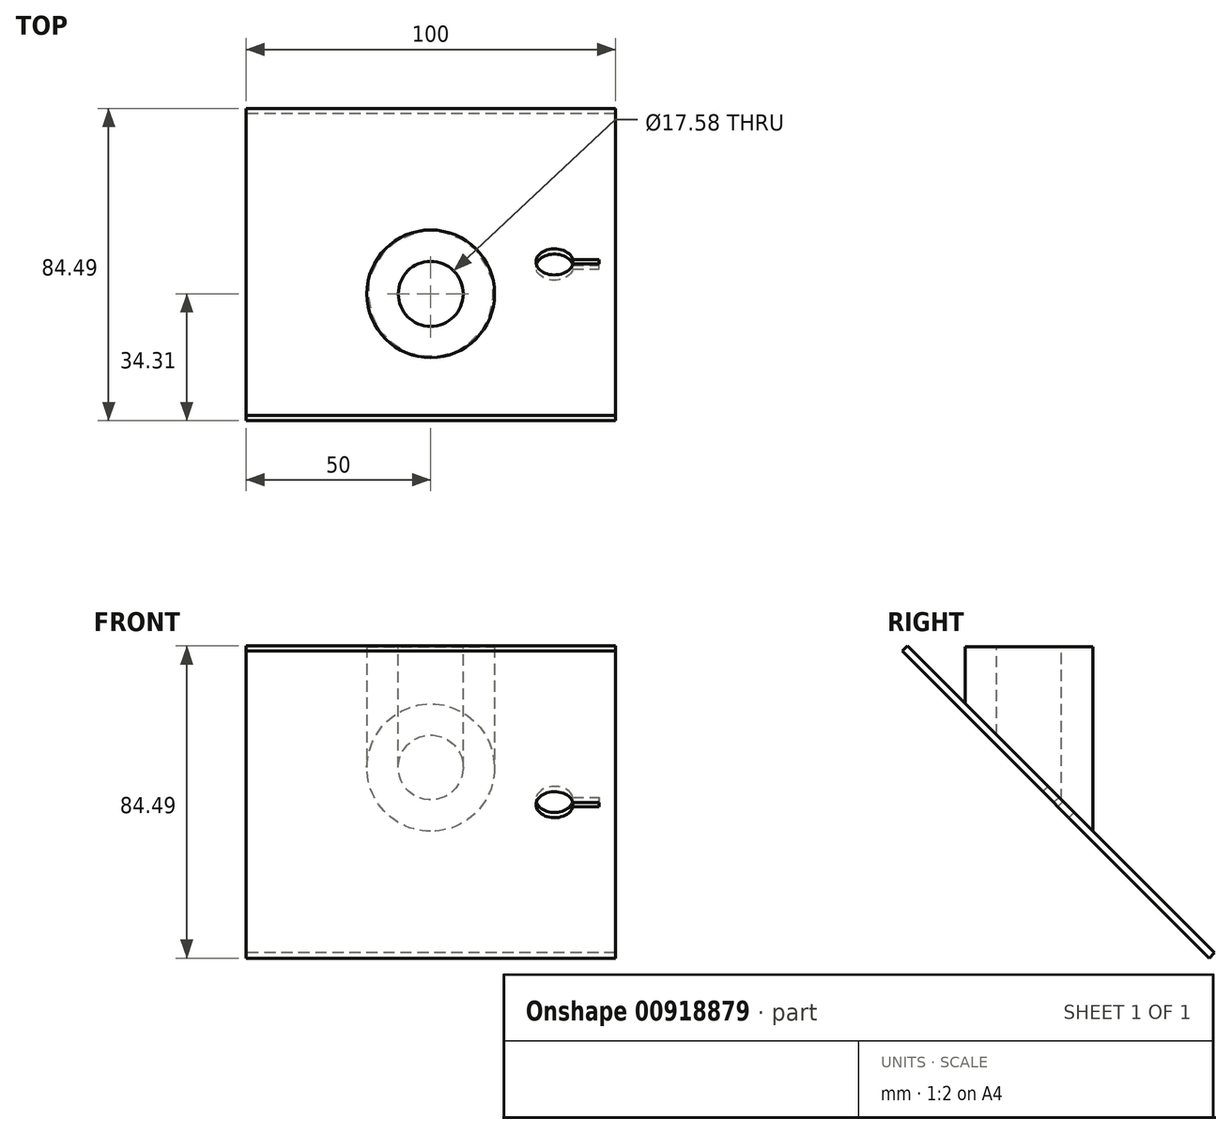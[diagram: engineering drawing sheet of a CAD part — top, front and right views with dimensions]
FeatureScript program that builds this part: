
annotation { "Feature Type Name" : "Feature", "Feature Type Description" : "" }
export const myFeature = defineFeature(function(context is Context, id is Id, definition is map)
    precondition{}
    {
        {
            var Q0;
            Q0=qCreatedBy(makeId("Top.planeOp"),FACE);
            var sketch = newSketch(context, id + "F0", { "sketchPlane" : qUnion([Q0])});
            skCircle(sketch, "E0", {"center": v(0, 0) * mm, "radius": 17.28 * mm});
            skSolve(sketch);
        }
        {
            var Q0;
            Q0=makeQuery(id+"F0.imprint","IMPRINT",FACE,{"disambiguationData":[TD([[makeQuery(id+"F0.imprint","IMPRINT",EDGE,{"derivedFrom":sQuery(id+"F0.wireOp",EDGE,"E0")}),1.0]])]});
            extrude(context, id + "F1", {"entities" : qUnion([Q0]), "depth" : 50 * mm, "offsetDistance" : 25 * mm});
        }
        {
            var Q0;
            Q0=makeQuery(id+"F1.opExtrude","CAP_FACE",FACE,{"disambiguationData":[OSD([sQuery(id+"F0.wireOp",EDGE,"E0")])],"isStart":false});
            var sketch = newSketch(context, id + "F2", { "sketchPlane" : qUnion([Q0])});
            skCircle(sketch, "E1", {"center": v(0, 0) * mm, "radius": 8.79 * mm});
            skSolve(sketch);
        }
        {
            var Q0;
            Q0=makeQuery(id+"F2.imprint","IMPRINT",FACE,{"disambiguationData":[TD([[makeQuery(id+"F2.imprint","IMPRINT",EDGE,{"derivedFrom":sQuery(id+"F2.wireOp",EDGE,"E1")}),1.0]])]});
            extrude(context, id + "F3", {"entities" : qUnion([Q0]), "operationType" : NewBodyOperationType.REMOVE, "oppositeDirection" : true, "depth" : 50 * mm, "offsetDistance" : 25 * mm});
        }
        {
            var Q0;
            Q0=qCreatedBy(makeId("Right.planeOp"),FACE);
            var sketch = newSketch(context, id + "F4", { "sketchPlane" : qUnion([Q0])});
            skLineSegment(sketch, "E2", {"start": v(-17.28, 17.28) * mm, "end": v(-17.28, 17.28) * mm});
            skLineSegment(sketch, "E3", {"start": v(0, 0) * mm, "end": v(0, 0) * mm});
            skLineSegment(sketch, "E4", {"start": v(-17.28, 0) * mm, "end": v(-17.28, 50) * mm});
            skLineSegment(sketch, "E5", {"start": v(17.28, 50) * mm, "end": v(17.28, 0) * mm});
            skPoint(sketch, "E6", {"position": v(-17.28, 34.57) * mm});
            skLineSegment(sketch, "E7", {"start": v(-17.28, 34.57) * mm, "end": v(17.28, 0) * mm});
            skLineSegment(sketch, "E8", {"start": v(17.28, 0) * mm, "end": v(-17.28, 0) * mm});
            skLineSegment(sketch, "E9", {"start": v(-17.28, 0) * mm, "end": v(-17.28, 34.57) * mm});
            skSolve(sketch);
        }
        {
            var Q0;
            Q0 = qSketchRegion(id + "F4", true);
            extrude(context, id + "F5", {"entities" : qUnion([Q0]), "operationType" : NewBodyOperationType.REMOVE, "endBound" : BoundingType.SYMMETRIC, "depth" : 40 * mm, "offsetDistance" : 25 * mm});
        }
        {
            var Q0;
            Q0=makeQuery(id+"F5.boolean.opBoolean","COPY",FACE,{"derivedFrom":makeQuery(id+"F5.opExtrude","SWEPT_FACE",FACE,{"disambiguationData":[OSD([sQuery(id+"F4.wireOp",EDGE,"E7")])]})});
            cPlane(context, id + "F6", {"entities" : qUnion([Q0]), "cplaneType" : CPlaneType.OFFSET, "offset" : 0 * mm, "width" : 150 * mm, "height" : 150 * mm});
        }
        {
            var Q0;
            Q0=qCreatedBy(id+"F6.planeOp",FACE);
            var sketch = newSketch(context, id + "F7", { "sketchPlane" : qUnion([Q0])});
            skLineSegment(sketch, "E10.bottom", {"start": v(50, -58.74) * mm, "end": v(-50, -58.74) * mm});
            skLineSegment(sketch, "E10.top", {"start": v(50, 58.74) * mm, "end": v(-50, 58.74) * mm});
            skLineSegment(sketch, "E10.left", {"start": v(50, -58.74) * mm, "end": v(50, 58.74) * mm});
            skLineSegment(sketch, "E10.right", {"start": v(-50, -58.74) * mm, "end": v(-50, 58.74) * mm});
            skPoint(sketch, "E10.middle", {"position": v(0, 0) * mm});
            skArc(sketch, "E11", {"start": v(38.4, 0.8) * mm, "mid": v(28.47, 0) * mm, "end": v(38.4, -0.8) * mm});
            skLineSegment(sketch, "E12.bottom", {"start": v(38.4, 0.8) * mm, "end": v(45.57, 0.8) * mm});
            skLineSegment(sketch, "E12.top", {"start": v(38.4, -0.8) * mm, "end": v(45.57, -0.8) * mm});
            skLineSegment(sketch, "E12.right", {"start": v(45.57, 0.8) * mm, "end": v(45.57, -0.8) * mm});
            skSolve(sketch);
        }
        {
            var Q0;
            Q0 = qSketchRegion(id + "F7", true);
            extrude(context, id + "F8", {"entities" : qUnion([Q0]), "operationType" : NewBodyOperationType.ADD, "depth" : 2 * mm, "offsetDistance" : 25 * mm});
        }
    });
